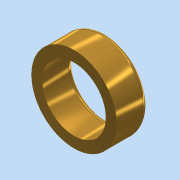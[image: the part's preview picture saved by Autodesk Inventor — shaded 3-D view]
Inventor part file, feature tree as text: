
AUTODESK INVENTOR PART (.ipt)
format: ipt  version: 2016 (Build 200138000, 138)  size: 126,464 bytes
history: native  units: mm
features: fillet x2, extrude x1, sketch x1
ambient origin geometry x8: Origin, YZ Plane, XZ Plane, XY Plane, X Axis, Y Axis, Z Axis, Center Point
bodies: Solid1 (feature_tree)
feature tree (4):
  extrude  "Extrusion1"  Depth=0.5mm
  fillet  "Fillet1"  Radius=0.5mm
  fillet  "Fillet2"  [1 undecoded]
  sketch  "Sketch1"  dims[d0=3.0mm d1=0.0mm d2=0.5mm d3=0.5mm]
note: 1 required parameter value undecoded (feature->parameter linkage not recoverable at this tier; creation-order binding heuristic only, values carry confidence <= 0.55)
